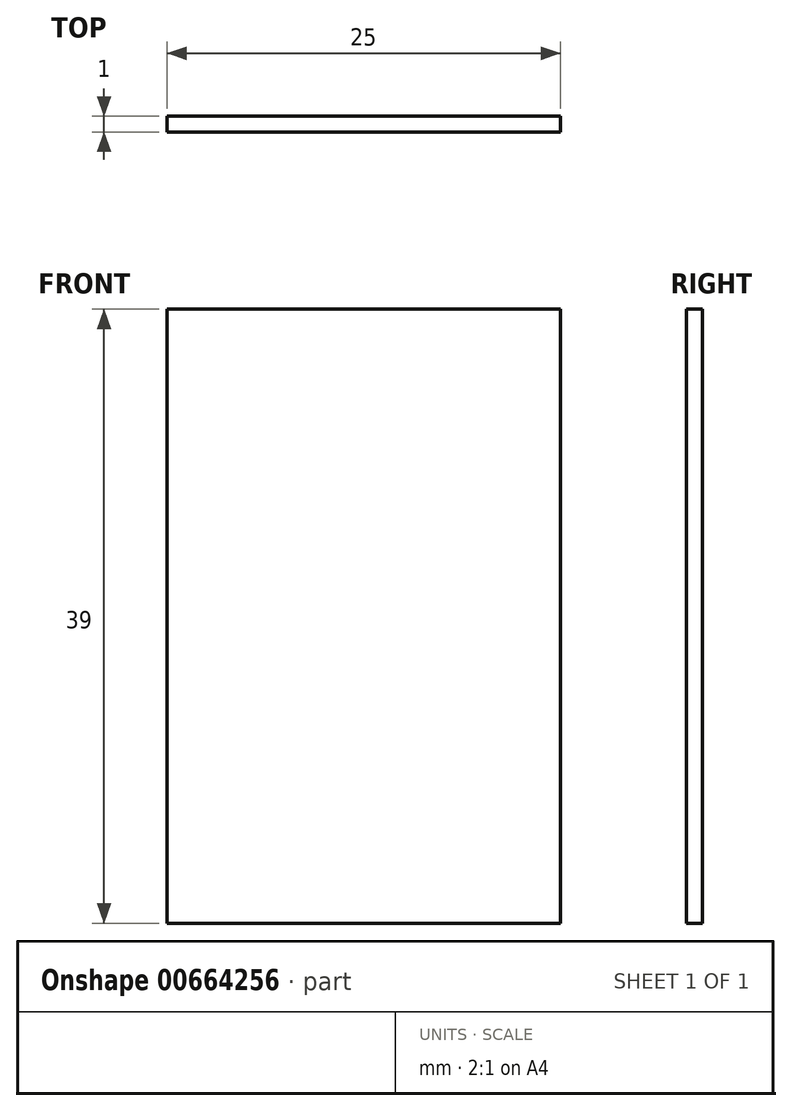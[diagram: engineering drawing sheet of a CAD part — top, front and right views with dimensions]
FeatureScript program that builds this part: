
annotation { "Feature Type Name" : "Feature", "Feature Type Description" : "" }
export const myFeature = defineFeature(function(context is Context, id is Id, definition is map)
    precondition{}
    {
        {
            var Q0;
            Q0=qCreatedBy(makeId("Front.planeOp"),FACE);
            var sketch = newSketch(context, id + "F0", { "sketchPlane" : qUnion([Q0])});
            skLineSegment(sketch, "E0.bottom", {"start": v(12.5, 19.5) * mm, "end": v(-12.5, 19.5) * mm});
            skLineSegment(sketch, "E0.top", {"start": v(12.5, -19.5) * mm, "end": v(-12.5, -19.5) * mm});
            skLineSegment(sketch, "E0.left", {"start": v(12.5, 19.5) * mm, "end": v(12.5, -19.5) * mm});
            skLineSegment(sketch, "E0.right", {"start": v(-12.5, 19.5) * mm, "end": v(-12.5, -19.5) * mm});
            skPoint(sketch, "E0.middle", {"position": v(0, 0) * mm});
            skSolve(sketch);
        }
        {
            var Q0;
            Q0=makeQuery(id+"F0.imprint","IMPRINT",FACE,{"disambiguationData":[TD([[makeQuery(id+"F0.imprint","IMPRINT",EDGE,{"derivedFrom":sQuery(id+"F0.wireOp",EDGE,"E0.bottom")}),1.0]])]});
            extrude(context, id + "F1", {"entities" : qUnion([Q0]), "depth" : 1 * mm, "offsetDistance" : 25 * mm});
        }
    });
